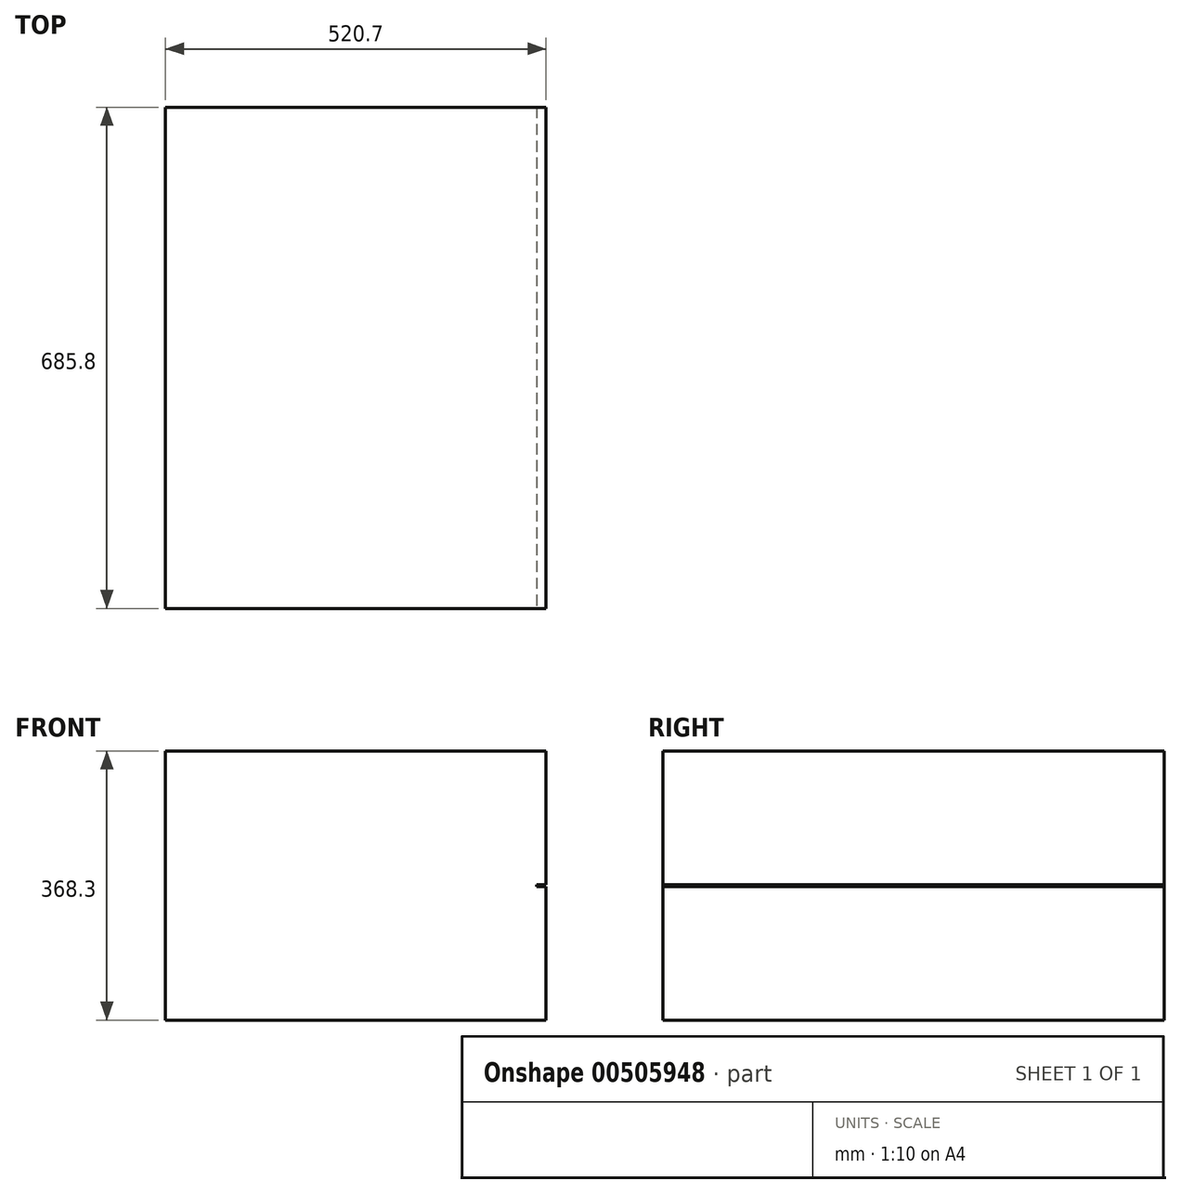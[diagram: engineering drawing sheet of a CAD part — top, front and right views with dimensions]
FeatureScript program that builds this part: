
annotation { "Feature Type Name" : "Feature", "Feature Type Description" : "" }
export const myFeature = defineFeature(function(context is Context, id is Id, definition is map)
    precondition{}
    {
        {
            var Q0;
            Q0=qCreatedBy(makeId("Top.planeOp"),FACE);
            var sketch = newSketch(context, id + "F0", { "sketchPlane" : qUnion([Q0])});
            skLineSegment(sketch, "E0.bottom", {"start": v(0, 0) * mm, "end": v(508, 0) * mm});
            skLineSegment(sketch, "E0.top", {"start": v(0, 685.8) * mm, "end": v(508, 685.8) * mm});
            skLineSegment(sketch, "E0.left", {"start": v(0, 0) * mm, "end": v(0, 685.8) * mm});
            skLineSegment(sketch, "E0.right", {"start": v(508, 0) * mm, "end": v(508, 685.8) * mm});
            skSolve(sketch);
        }
        {
            var Q0;
            Q0=makeQuery(id+"F0.imprint","IMPRINT",FACE,{"disambiguationData":[TD([[makeQuery(id+"F0.imprint","IMPRINT",EDGE,{"derivedFrom":sQuery(id+"F0.wireOp",EDGE,"E0.bottom")}),1.0]])]});
            extrude(context, id + "F1", {"entities" : qUnion([Q0]), "depth" : 368.3 * mm, "offsetDistance" : 25.4 * mm});
        }
        {
            var Q0;
            Q0=makeQuery(id+"F1.opExtrude","SWEPT_FACE",FACE,{"disambiguationData":[OSD([sQuery(id+"F0.wireOp",EDGE,"E0.right")])]});
            var sketch = newSketch(context, id + "F2", { "sketchPlane" : qUnion([Q0])});
            skLineSegment(sketch, "E1.bottom", {"start": v(0, 0) * mm, "end": v(685.8, 0) * mm});
            skLineSegment(sketch, "E1.top", {"start": v(0, 182.88) * mm, "end": v(685.8, 182.88) * mm});
            skLineSegment(sketch, "E1.left", {"start": v(0, 0) * mm, "end": v(0, 182.88) * mm});
            skLineSegment(sketch, "E1.right", {"start": v(685.8, 0) * mm, "end": v(685.8, 182.88) * mm});
            skSolve(sketch);
        }
        {
            var Q0;
            Q0 = qSketchRegion(id + "F2", true);
            extrude(context, id + "F3", {"entities" : qUnion([Q0]), "operationType" : NewBodyOperationType.ADD, "depth" : 12.7 * mm, "offsetDistance" : 25.4 * mm});
        }
        {
            var Q0;
            Q0=makeQuery(id+"F1.opExtrude","SWEPT_FACE",FACE,{"disambiguationData":[OSD([sQuery(id+"F0.wireOp",EDGE,"E0.right")])]});
            var sketch = newSketch(context, id + "F4", { "sketchPlane" : qUnion([Q0])});
            skLineSegment(sketch, "E2.bottom", {"start": v(685.8, 368.3) * mm, "end": v(0, 368.3) * mm});
            skLineSegment(sketch, "E2.top", {"start": v(685.8, 185.42) * mm, "end": v(0, 185.42) * mm});
            skLineSegment(sketch, "E2.left", {"start": v(685.8, 368.3) * mm, "end": v(685.8, 185.42) * mm});
            skLineSegment(sketch, "E2.right", {"start": v(0, 368.3) * mm, "end": v(0, 185.42) * mm});
            skSolve(sketch);
        }
        {
            var Q0;
            Q0=makeQuery(id+"F4.imprint","IMPRINT",FACE,{"disambiguationData":[TD([[makeQuery(id+"F4.imprint","IMPRINT",EDGE,{"derivedFrom":sQuery(id+"F4.wireOp",EDGE,"E2.bottom")}),-1.0]])]});
            extrude(context, id + "F5", {"entities" : qUnion([Q0]), "operationType" : NewBodyOperationType.ADD, "depth" : 12.7 * mm, "offsetDistance" : 25.4 * mm});
        }
    });
